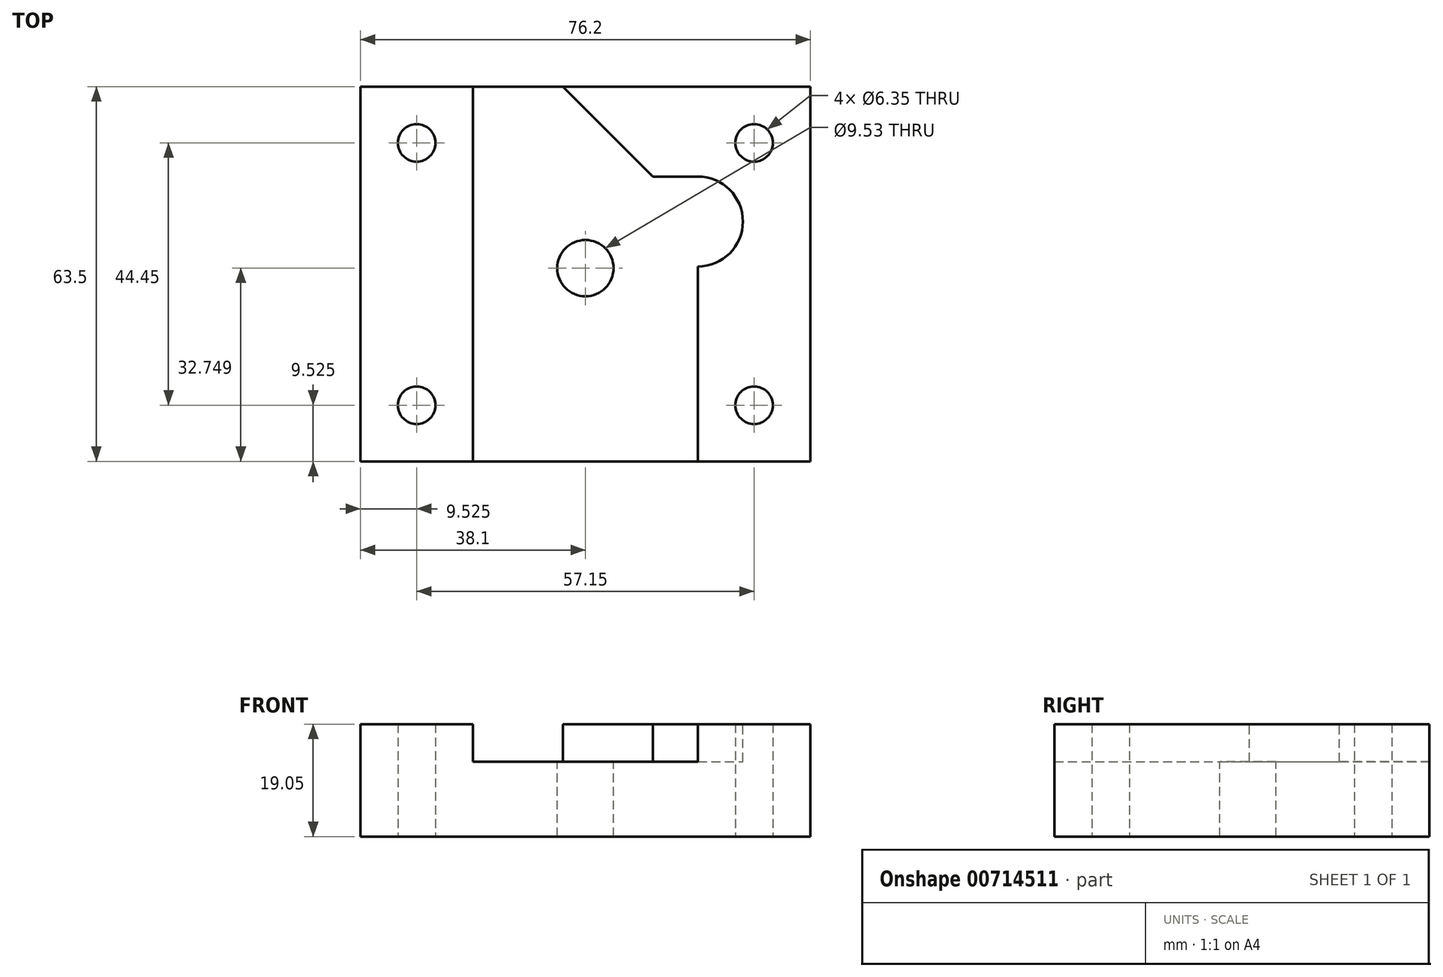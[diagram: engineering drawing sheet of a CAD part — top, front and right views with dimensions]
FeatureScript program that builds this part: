
annotation { "Feature Type Name" : "Feature", "Feature Type Description" : "" }
export const myFeature = defineFeature(function(context is Context, id is Id, definition is map)
    precondition{}
    {
        {
            var Q0;
            Q0=qCreatedBy(makeId("Top.planeOp"),FACE);
            var sketch = newSketch(context, id + "F0", { "sketchPlane" : qUnion([Q0])});
            skLineSegment(sketch, "E0.bottom", {"start": v(0, 0) * mm, "end": v(76.2, 0) * mm});
            skLineSegment(sketch, "E0.top", {"start": v(0, 63.5) * mm, "end": v(76.2, 63.5) * mm});
            skLineSegment(sketch, "E0.left", {"start": v(0, 0) * mm, "end": v(0, 63.5) * mm});
            skLineSegment(sketch, "E0.right", {"start": v(76.2, 0) * mm, "end": v(76.2, 63.5) * mm});
            skCircle(sketch, "E1", {"center": v(9.52, 9.52) * mm, "radius": 3.18 * mm});
            skCircle(sketch, "E2", {"center": v(9.52, 53.98) * mm, "radius": 3.18 * mm});
            skCircle(sketch, "E3", {"center": v(66.67, 53.98) * mm, "radius": 3.18 * mm});
            skCircle(sketch, "E4", {"center": v(66.67, 9.52) * mm, "radius": 3.18 * mm});
            skSolve(sketch);
        }
        {
            var Q0;
            Q0=makeQuery(id+"F0.imprint","IMPRINT",FACE,{"disambiguationData":[TD([[makeQuery(id+"F0.imprint","IMPRINT",EDGE,{"derivedFrom":sQuery(id+"F0.wireOp",EDGE,"E0.bottom")}),1.0]])]});
            extrude(context, id + "F1", {"entities" : qUnion([Q0]), "depth" : 19.05 * mm, "offsetDistance" : 25.4 * mm});
        }
        {
            var Q0;
            Q0=makeQuery(id+"F1.opExtrude","CAP_FACE",FACE,{"disambiguationData":[OSD([sQuery(id+"F0.wireOp",EDGE,"E0.bottom"),sQuery(id+"F0.wireOp",EDGE,"E0.top"),sQuery(id+"F0.wireOp",EDGE,"E0.left"),sQuery(id+"F0.wireOp",EDGE,"E0.right"),sQuery(id+"F0.wireOp",EDGE,"E1"),sQuery(id+"F0.wireOp",EDGE,"E2"),sQuery(id+"F0.wireOp",EDGE,"E3"),sQuery(id+"F0.wireOp",EDGE,"E4")])],"isStart":false});
            var sketch = newSketch(context, id + "F2", { "sketchPlane" : qUnion([Q0])});
            skLineSegment(sketch, "E5.bottom", {"start": v(19.05, -10.16) * mm, "end": v(57.15, -10.16) * mm});
            skLineSegment(sketch, "E5.left", {"start": v(19.05, -10.16) * mm, "end": v(19.05, 78.74) * mm});
            skLineSegment(sketch, "E5.right", {"start": v(57.15, -10.16) * mm, "end": v(57.15, 33.02) * mm});
            skLineSegment(sketch, "E6", {"start": v(19.05, 78.74) * mm, "end": v(49.53, 48.26) * mm});
            skCircle(sketch, "E7", {"center": v(38.1, 32.75) * mm, "radius": 4.76 * mm});
            skLineSegment(sketch, "E8", {"start": v(19.05, 63.5) * mm, "end": v(34.3, 63.5) * mm, "construction": true});
            skLineSegment(sketch, "E9", {"start": v(19.05, 63.5) * mm, "end": v(0, 63.5) * mm});
            skLineSegment(sketch, "E10", {"start": v(0, 63.5) * mm, "end": v(0, 0) * mm});
            skLineSegment(sketch, "E11", {"start": v(0, 0) * mm, "end": v(19.05, 0) * mm});
            skLineSegment(sketch, "E12", {"start": v(34.3, 63.5) * mm, "end": v(76.2, 63.5) * mm});
            skLineSegment(sketch, "E13", {"start": v(76.2, 63.5) * mm, "end": v(76.2, 0) * mm});
            skLineSegment(sketch, "E14", {"start": v(76.2, 0) * mm, "end": v(57.15, 0) * mm});
            skArc(sketch, "E15", {"start": v(57.15, 33.02) * mm, "mid": v(64.77, 40.64) * mm, "end": v(57.15, 48.26) * mm});
            skLineSegment(sketch, "E16", {"start": v(57.15, 48.26) * mm, "end": v(49.53, 48.26) * mm});
            skSolve(sketch);
        }
        {
            var Q0;
            Q0=makeQuery(id+"F2.imprint","IMPRINT",FACE,{"disambiguationData":[TD([[makeQuery(id+"F2.imprint","IMPRINT",EDGE,{"derivedFrom":sQuery(id+"F2.wireOp",EDGE,"E7")}),-1.0]])]});
            var Q1;
            Q1=makeQuery(id+"F2.imprint","IMPRINT",FACE,{"disambiguationData":[TD([[makeQuery(id+"F2.imprint","IMPRINT",EDGE,{"derivedFrom":sQuery(id+"F2.wireOp",EDGE,"E7")}),1.0]])]});
            extrude(context, id + "F3", {"entities" : qUnion([Q0, Q1]), "operationType" : NewBodyOperationType.REMOVE, "oppositeDirection" : true, "depth" : 6.35 * mm, "offsetDistance" : 25.4 * mm});
        }
        {
            var Q0;
            Q0=makeQuery(id+"F3.boolean.opBoolean","COPY",FACE,{"derivedFrom":makeQuery(id+"F3.opExtrude","CAP_FACE",FACE,{"disambiguationData":[OSD([sQuery(id+"F0.wireOp",EDGE,"E0.bottom"),sQuery(id+"F0.wireOp",EDGE,"E0.top"),sQuery(id+"F2.wireOp",EDGE,"E5.left"),sQuery(id+"F2.wireOp",EDGE,"E5.right"),sQuery(id+"F2.wireOp",EDGE,"E6")])],"isStart":false})});
            var sketch = newSketch(context, id + "F4", { "sketchPlane" : qUnion([Q0])});
            skLineSegment(sketch, "E17.0.0", {"start": v(49.53, 48.26) * mm, "end": v(34.3, 63.5) * mm});
            skLineSegment(sketch, "E17.0.1", {"start": v(34.3, 63.5) * mm, "end": v(19.05, 63.5) * mm});
            skLineSegment(sketch, "E17.0.2", {"start": v(19.05, 63.5) * mm, "end": v(19.05, 0) * mm});
            skLineSegment(sketch, "E17.0.3", {"start": v(19.05, 0) * mm, "end": v(57.15, 0) * mm});
            skLineSegment(sketch, "E17.0.4", {"start": v(57.15, 0) * mm, "end": v(57.15, 40.64) * mm});
            skCircle(sketch, "E18", {"center": v(38.1, 32.75) * mm, "radius": 4.76 * mm});
            skSolve(sketch);
        }
        {
            var Q0;
            Q0=makeQuery(id+"F4.imprint","IMPRINT",FACE,{"disambiguationData":[TD([[makeQuery(id+"F4.imprint","IMPRINT",EDGE,{"derivedFrom":sQuery(id+"F4.wireOp",EDGE,"E18")}),1.0]])]});
            extrude(context, id + "F5", {"entities" : qUnion([Q0]), "operationType" : NewBodyOperationType.REMOVE, "endBound" : BoundingType.THROUGH_ALL, "oppositeDirection" : true, "depth" : 25.4 * mm, "offsetDistance" : 25.4 * mm});
        }
    });
